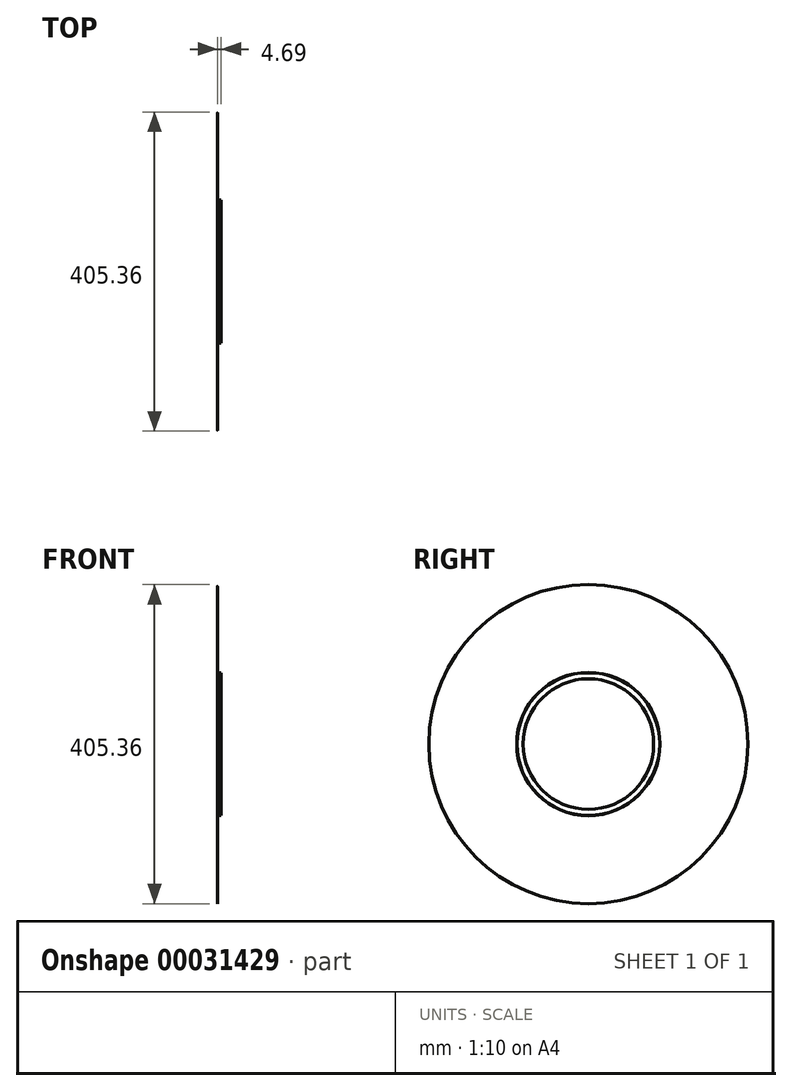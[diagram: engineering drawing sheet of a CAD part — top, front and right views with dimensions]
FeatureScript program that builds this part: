
annotation { "Feature Type Name" : "Feature", "Feature Type Description" : "" }
export const myFeature = defineFeature(function(context is Context, id is Id, definition is map)
    precondition{}
    {
        {
            var Q0;
            Q0=qCreatedBy(makeId("Front.planeOp"),FACE);
            var sketch = newSketch(context, id + "F0", { "sketchPlane" : qUnion([Q0])});
            skLineSegment(sketch, "E0.rect.bottom", {"start": v(100, 100) * mm, "end": v(-100, 100) * mm});
            skLineSegment(sketch, "E0.rect.top", {"start": v(100, -100) * mm, "end": v(-100, -100) * mm});
            skLineSegment(sketch, "E0.rect.left", {"start": v(100, 100) * mm, "end": v(100, -100) * mm});
            skLineSegment(sketch, "E0.rect.right", {"start": v(-100, 100) * mm, "end": v(-100, -100) * mm});
            skPoint(sketch, "E0.rect.middle", {"position": v(0, 0) * mm});
            skLineSegment(sketch, "E1", {"start": v(-100, 100) * mm, "end": v(-68, 100) * mm});
            skLineSegment(sketch, "E2", {"start": v(-68, 100) * mm, "end": v(-60, 100) * mm});
            skLineSegment(sketch, "E3", {"start": v(-60, 100) * mm, "end": v(-52, 100) * mm});
            skLineSegment(sketch, "E4", {"start": v(-52, 100) * mm, "end": v(-44, 100) * mm});
            skLineSegment(sketch, "E5", {"start": v(-44, 100) * mm, "end": v(-36, 100) * mm});
            skLineSegment(sketch, "E6", {"start": v(-36, 100) * mm, "end": v(-28, 100) * mm});
            skLineSegment(sketch, "E7", {"start": v(-28, 100) * mm, "end": v(-20, 100) * mm});
            skLineSegment(sketch, "E8", {"start": v(-20, 100) * mm, "end": v(-12, 100) * mm});
            skLineSegment(sketch, "E9", {"start": v(-12, 100) * mm, "end": v(-4, 100) * mm});
            skLineSegment(sketch, "E10", {"start": v(-4, 100) * mm, "end": v(4, 100) * mm});
            skLineSegment(sketch, "E11", {"start": v(4, 100) * mm, "end": v(12, 100) * mm});
            skLineSegment(sketch, "E12", {"start": v(12, 100) * mm, "end": v(20, 100) * mm});
            skLineSegment(sketch, "E13", {"start": v(20, 100) * mm, "end": v(28, 100) * mm});
            skLineSegment(sketch, "E14", {"start": v(28, 100) * mm, "end": v(36, 100) * mm});
            skLineSegment(sketch, "E15", {"start": v(36, 100) * mm, "end": v(44, 100) * mm});
            skLineSegment(sketch, "E16", {"start": v(44, 100) * mm, "end": v(52, 100) * mm});
            skLineSegment(sketch, "E17", {"start": v(52, 100) * mm, "end": v(60, 100) * mm});
            skLineSegment(sketch, "E18", {"start": v(60, 100) * mm, "end": v(68, 100) * mm});
            skCircle(sketch, "E19", {"center": v(0, 0) * mm, "radius": 91.07 * mm, "construction": true});
            skCircle(sketch, "E20", {"center": v(0, 0) * mm, "radius": 83.33 * mm, "construction": true});
            skCircle(sketch, "E21", {"center": v(0, 0) * mm, "radius": 37.2 * mm, "construction": true});
            skLineSegment(sketch, "E22", {"start": v(4, 100) * mm, "end": v(4, 90.98) * mm});
            skLineSegment(sketch, "E23", {"start": v(68, 100) * mm, "end": v(68, 94) * mm});
            skLineSegment(sketch, "E24", {"start": v(60, 100) * mm, "end": v(60, 94) * mm});
            skLineSegment(sketch, "E25", {"start": v(52, 100) * mm, "end": v(52, 94) * mm});
            skLineSegment(sketch, "E26", {"start": v(44, 100) * mm, "end": v(44, 94) * mm});
            skLineSegment(sketch, "E27", {"start": v(36, 100) * mm, "end": v(36, 94) * mm});
            skLineSegment(sketch, "E28", {"start": v(28, 100) * mm, "end": v(28, 94) * mm});
            skLineSegment(sketch, "E29", {"start": v(20, 100) * mm, "end": v(20, 94) * mm});
            skLineSegment(sketch, "E30", {"start": v(12, 100) * mm, "end": v(12, 94) * mm});
            skLineSegment(sketch, "E31", {"start": v(68, 94) * mm, "end": v(50.35, 75.88) * mm});
            skLineSegment(sketch, "E32", {"start": v(60, 94) * mm, "end": v(46.03, 78.57) * mm});
            skLineSegment(sketch, "E33", {"start": v(52, 94) * mm, "end": v(41.38, 81.12) * mm});
            skLineSegment(sketch, "E34", {"start": v(44, 94) * mm, "end": v(37, 83.21) * mm});
            skLineSegment(sketch, "E35", {"start": v(36, 94) * mm, "end": v(31.15, 85.57) * mm});
            skLineSegment(sketch, "E36", {"start": v(28, 94) * mm, "end": v(24.47, 87.71) * mm});
            skLineSegment(sketch, "E37", {"start": v(20, 94) * mm, "end": v(17.48, 89.37) * mm});
            skLineSegment(sketch, "E38", {"start": v(12, 94) * mm, "end": v(10.94, 90.4) * mm});
            skLineSegment(sketch, "E39", {"start": v(4, 90.98) * mm, "end": v(8.69, 90.65) * mm});
            skLineSegment(sketch, "E40", {"start": v(8.69, 90.65) * mm, "end": v(8.69, 82.87) * mm});
            skLineSegment(sketch, "E41", {"start": v(8.69, 82.87) * mm, "end": v(4, 83.23) * mm});
            skLineSegment(sketch, "E42", {"start": v(10.94, 90.4) * mm, "end": v(15.19, 89.8) * mm});
            skLineSegment(sketch, "E43", {"start": v(15.19, 89.8) * mm, "end": v(15.19, 81.93) * mm});
            skLineSegment(sketch, "E44", {"start": v(15.19, 81.93) * mm, "end": v(11.55, 82.52) * mm});
            skLineSegment(sketch, "E45", {"start": v(17.48, 89.37) * mm, "end": v(22, 88.37) * mm});
            skLineSegment(sketch, "E46", {"start": v(22, 88.37) * mm, "end": v(21.04, 80.63) * mm});
            skLineSegment(sketch, "E47", {"start": v(21.04, 80.63) * mm, "end": v(17.6, 81.45) * mm});
            skLineSegment(sketch, "E48", {"start": v(24.47, 87.71) * mm, "end": v(28.72, 86.42) * mm});
            skLineSegment(sketch, "E49", {"start": v(28.72, 86.42) * mm, "end": v(27.24, 78.75) * mm});
            skLineSegment(sketch, "E50", {"start": v(27.24, 78.75) * mm, "end": v(23.76, 79.87) * mm});
            skLineSegment(sketch, "E51", {"start": v(31.15, 85.57) * mm, "end": v(34.97, 84.08) * mm});
            skLineSegment(sketch, "E52", {"start": v(34.97, 84.08) * mm, "end": v(33.12, 76.46) * mm});
            skLineSegment(sketch, "E53", {"start": v(33.12, 76.46) * mm, "end": v(29.89, 77.78) * mm});
            skLineSegment(sketch, "E54", {"start": v(37, 83.21) * mm, "end": v(39.54, 82.03) * mm});
            skLineSegment(sketch, "E55", {"start": v(39.54, 82.03) * mm, "end": v(37.99, 74.16) * mm});
            skLineSegment(sketch, "E56", {"start": v(37.99, 74.16) * mm, "end": v(35.13, 75.56) * mm});
            skLineSegment(sketch, "E57", {"start": v(41.38, 81.12) * mm, "end": v(44.17, 79.64) * mm});
            skLineSegment(sketch, "E58", {"start": v(44.17, 79.64) * mm, "end": v(42.57, 71.63) * mm});
            skLineSegment(sketch, "E59", {"start": v(42.57, 71.63) * mm, "end": v(40.04, 73.08) * mm});
            skLineSegment(sketch, "E60", {"start": v(46.03, 78.57) * mm, "end": v(48.68, 76.96) * mm});
            skLineSegment(sketch, "E61", {"start": v(48.68, 76.96) * mm, "end": v(47.1, 68.74) * mm});
            skLineSegment(sketch, "E62", {"start": v(47.1, 68.74) * mm, "end": v(44.52, 70.44) * mm});
            skLineSegment(sketch, "E63", {"start": v(50.35, 75.88) * mm, "end": v(54.15, 73.22) * mm});
            skLineSegment(sketch, "E64", {"start": v(54.15, 73.22) * mm, "end": v(52.4, 64.79) * mm});
            skLineSegment(sketch, "E65", {"start": v(52.4, 64.79) * mm, "end": v(49.27, 67.2) * mm});
            skLineSegment(sketch, "E66", {"start": v(4, 83.23) * mm, "end": v(4, 0) * mm});
            skLineSegment(sketch, "E67", {"start": v(49.27, 67.2) * mm, "end": v(21.1, 30.63) * mm});
            skLineSegment(sketch, "E68", {"start": v(21.1, 30.63) * mm, "end": v(4, 36.98) * mm});
            skLineSegment(sketch, "E69", {"start": v(11.55, 82.52) * mm, "end": v(6.16, 36.18) * mm});
            skLineSegment(sketch, "E70", {"start": v(17.6, 81.45) * mm, "end": v(8.04, 35.49) * mm});
            skLineSegment(sketch, "E71", {"start": v(23.76, 79.87) * mm, "end": v(9.34, 35) * mm});
            skLineSegment(sketch, "E72", {"start": v(29.89, 77.78) * mm, "end": v(10.72, 34.49) * mm});
            skLineSegment(sketch, "E73", {"start": v(35.13, 75.56) * mm, "end": v(12.55, 33.8) * mm});
            skLineSegment(sketch, "E74", {"start": v(40.04, 73.08) * mm, "end": v(14.38, 33.13) * mm});
            skLineSegment(sketch, "E75", {"start": v(44.52, 70.44) * mm, "end": v(17.38, 32.02) * mm});
            skLineSegment(sketch, "E76", {"start": v(4, 100) * mm, "end": v(4, 202.68) * mm});
            skLineSegment(sketch, "E77", {"start": v(12, 100) * mm, "end": v(12, 202.68) * mm});
            skLineSegment(sketch, "E78", {"start": v(20, 100) * mm, "end": v(20, 202.68) * mm});
            skLineSegment(sketch, "E79", {"start": v(28, 100) * mm, "end": v(28, 202.68) * mm});
            skLineSegment(sketch, "E80", {"start": v(36, 100) * mm, "end": v(36, 100) * mm});
            skLineSegment(sketch, "E81", {"start": v(36, 100) * mm, "end": v(36, 202.68) * mm});
            skLineSegment(sketch, "E82", {"start": v(44, 100) * mm, "end": v(44, 202.68) * mm});
            skLineSegment(sketch, "E83", {"start": v(52, 100) * mm, "end": v(52, 202.68) * mm});
            skLineSegment(sketch, "E84", {"start": v(60, 100) * mm, "end": v(60, 202.68) * mm});
            skLineSegment(sketch, "E85", {"start": v(68, 100) * mm, "end": v(68, 202.68) * mm});
            skSolve(sketch);
        }
        {
            var Q0;
            Q0=qCreatedBy(makeId("Top.planeOp"),FACE);
            var sketch = newSketch(context, id + "F1", { "sketchPlane" : qUnion([Q0])});
            skLineSegment(sketch, "E86", {"start": v(0, 0) * mm, "end": v(157.65, 0) * mm});
            skLineSegment(sketch, "E87", {"start": v(157.65, 0) * mm, "end": v(-165.99, 0) * mm});
            skSolve(sketch);
        }
        {
            var Q0;
            Q0=sQuery(id+"F0.wireOp",EDGE,"E22");
            var Q1;
            Q1=sQuery(id+"F0.wireOp",EDGE,"E39");
            var Q2;
            Q2=sQuery(id+"F0.wireOp",EDGE,"E40");
            var Q3;
            Q3=sQuery(id+"F0.wireOp",EDGE,"E41");
            var Q4;
            Q4=sQuery(id+"F0.wireOp",EDGE,"E66");
            var Q5;
            Q5=sQuery(id+"F0.wireOp",EDGE,"E76");
            var Q6;
            Q6=sQuery(id+"F1.wireOp",EDGE,"E86");
            revolve(context, id + "F2", {"bodyType" : ToolBodyType.SURFACE, "surfaceEntities" : qUnion([Q0, Q1, Q2, Q3, Q4, Q5]), "axis" : qUnion([Q6]), "revolveType" : RevolveType.FULL});
        }
    });
